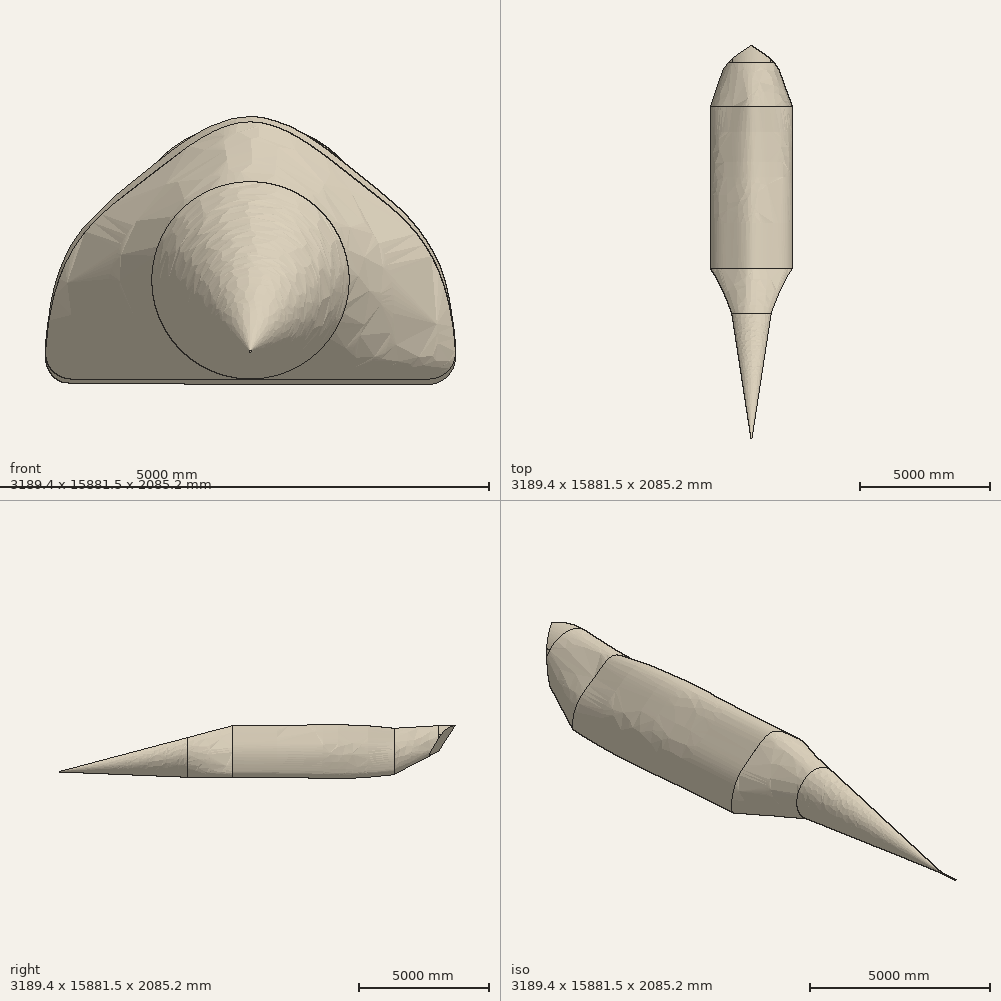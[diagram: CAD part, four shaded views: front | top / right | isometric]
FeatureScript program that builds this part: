
annotation { "Feature Type Name" : "Feature", "Feature Type Description" : "" }
export const myFeature = defineFeature(function(context is Context, id is Id, definition is map)
    precondition{}
    {
        {
            var Q0;
            Q0=qCreatedBy(makeId("Front.planeOp"),FACE);
            cPlane(context, id + "F0", {"entities" : qUnion([Q0]), "cplaneType" : CPlaneType.OFFSET, "offset" : 1750 * mm, "width" : 150 * mm, "height" : 150 * mm});
        }
        {
            var Q0;
            Q0=qCreatedBy(id+"F0.planeOp",FACE);
            var sketch = newSketch(context, id + "F1", { "sketchPlane" : qUnion([Q0])});
            skLineSegment(sketch, "E0.top", {"start": v(-1394.2, -1000) * mm, "end": v(1394.2, -1000) * mm});
            skPoint(sketch, "E0.middle", {"position": v(0, 0) * mm});
            skFitSpline(sketch, "E1", {"points": [v(-1600, -1000) * mm, v(-848, 530) * mm, v(0, 1000) * mm, v(848, 530) * mm, v(1600, -1000) * mm], "startDerivative": vector(0, 10524.75) * mm, "endDerivative": vector(0, -10524.75) * mm});
            skArc(sketch, "E2", {"start": v(-735.27, 618.52) * mm, "mid": v(-1273.27, 435.52) * mm, "end": v(-1440.68, -107.53) * mm});
            skArc(sketch, "E3", {"start": v(1440.68, -107.53) * mm, "mid": v(1273.27, 435.52) * mm, "end": v(735.27, 618.52) * mm});
            skFitSpline(sketch, "E4.trimOffspring", {"points": [v(-1600, -1000) * mm, v(-848, 530) * mm, v(0, 1000) * mm, v(848, 530) * mm, v(1600, -1000) * mm], "startDerivative": vector(0, 10524.75) * mm, "endDerivative": vector(0, -10524.75) * mm});
            skFitSpline(sketch, "E5.trimOffspring", {"points": [v(-1600, -1000) * mm, v(-848, 530) * mm, v(0, 1000) * mm, v(848, 530) * mm, v(1600, -1000) * mm], "startDerivative": vector(0, 10524.75) * mm, "endDerivative": vector(0, -10524.75) * mm});
            skArc(sketch, "E6.filletArc", {"start": v(-1593.82, -787.83) * mm, "mid": v(-1539.85, -937.05) * mm, "end": v(-1394.2, -1000) * mm});
            skArc(sketch, "E7.filletArc", {"start": v(1394.2, -1000) * mm, "mid": v(1539.85, -937.05) * mm, "end": v(1593.82, -787.83) * mm});
            skSolve(sketch);
        }
        {
            var Q0;
            Q0=qCreatedBy(makeId("Front.planeOp"),FACE);
            var sketch = newSketch(context, id + "F2", { "sketchPlane" : qUnion([Q0])});
            skLineSegment(sketch, "E8.top", {"start": v(-1394.2, -1000) * mm, "end": v(1394.2, -1000) * mm});
            skPoint(sketch, "E8.middle", {"position": v(0, 0) * mm});
            skFitSpline(sketch, "E9", {"points": [v(-1600, -1000) * mm, v(-848, 530) * mm, v(0, 1000) * mm, v(848, 530) * mm, v(1600, -1000) * mm], "startDerivative": vector(0, 10524.75) * mm, "endDerivative": vector(0, -10524.75) * mm});
            skArc(sketch, "E10", {"start": v(-735.27, 618.52) * mm, "mid": v(-1273.27, 435.52) * mm, "end": v(-1440.68, -107.53) * mm});
            skArc(sketch, "E11", {"start": v(1440.68, -107.53) * mm, "mid": v(1273.27, 435.52) * mm, "end": v(735.27, 618.52) * mm});
            skFitSpline(sketch, "E12.trimOffspring", {"points": [v(-1600, -1000) * mm, v(-848, 530) * mm, v(0, 1000) * mm, v(848, 530) * mm, v(1600, -1000) * mm], "startDerivative": vector(0, 10524.75) * mm, "endDerivative": vector(0, -10524.75) * mm});
            skFitSpline(sketch, "E13.trimOffspring", {"points": [v(-1600, -1000) * mm, v(-848, 530) * mm, v(0, 1000) * mm, v(848, 530) * mm, v(1600, -1000) * mm], "startDerivative": vector(0, 10524.75) * mm, "endDerivative": vector(0, -10524.75) * mm});
            skArc(sketch, "E14.filletArc", {"start": v(-1593.82, -787.83) * mm, "mid": v(-1539.85, -937.05) * mm, "end": v(-1394.2, -1000) * mm});
            skArc(sketch, "E15.filletArc", {"start": v(1394.2, -1000) * mm, "mid": v(1539.85, -937.05) * mm, "end": v(1593.82, -787.83) * mm});
            skSolve(sketch);
        }
        {
            var Q0;
            Q0=qCreatedBy(makeId("Front.planeOp"),FACE);
            cPlane(context, id + "F3", {"entities" : qUnion([Q0]), "cplaneType" : CPlaneType.OFFSET, "offset" : 3500 * mm, "oppositeDirection" : true, "width" : 150 * mm, "height" : 150 * mm});
        }
        {
            var Q0;
            Q0=qCreatedBy(id+"F3.planeOp",FACE);
            var sketch = newSketch(context, id + "F4", { "sketchPlane" : qUnion([Q0])});
            skLineSegment(sketch, "E16.top", {"start": v(-1394.2, -1000) * mm, "end": v(1394.2, -1000) * mm});
            skPoint(sketch, "E16.middle", {"position": v(0, 0) * mm});
            skFitSpline(sketch, "E17", {"points": [v(-1600, -1000) * mm, v(-848, 530) * mm, v(0, 1000) * mm, v(848, 530) * mm, v(1600, -1000) * mm], "startDerivative": vector(0, 10524.75) * mm, "endDerivative": vector(0, -10524.75) * mm});
            skArc(sketch, "E18", {"start": v(-735.27, 618.52) * mm, "mid": v(-1273.27, 435.52) * mm, "end": v(-1440.68, -107.53) * mm});
            skArc(sketch, "E19", {"start": v(1440.68, -107.53) * mm, "mid": v(1273.27, 435.52) * mm, "end": v(735.27, 618.52) * mm});
            skFitSpline(sketch, "E20.trimOffspring", {"points": [v(-1600, -1000) * mm, v(-848, 530) * mm, v(0, 1000) * mm, v(848, 530) * mm, v(1600, -1000) * mm], "startDerivative": vector(0, 10524.75) * mm, "endDerivative": vector(0, -10524.75) * mm});
            skFitSpline(sketch, "E21.trimOffspring", {"points": [v(-1600, -1000) * mm, v(-848, 530) * mm, v(0, 1000) * mm, v(848, 530) * mm, v(1600, -1000) * mm], "startDerivative": vector(0, 10524.75) * mm, "endDerivative": vector(0, -10524.75) * mm});
            skArc(sketch, "E22.filletArc", {"start": v(-1593.82, -787.83) * mm, "mid": v(-1539.85, -937.05) * mm, "end": v(-1394.2, -1000) * mm});
            skArc(sketch, "E23.filletArc", {"start": v(1394.2, -1000) * mm, "mid": v(1539.85, -937.05) * mm, "end": v(1593.82, -787.83) * mm});
            skSolve(sketch);
        }
        {
            var Q0;
            Q0=qCreatedBy(makeId("Front.planeOp"),FACE);
            cPlane(context, id + "F5", {"entities" : qUnion([Q0]), "cplaneType" : CPlaneType.OFFSET, "offset" : 4500 * mm, "oppositeDirection" : true, "width" : 150 * mm, "height" : 150 * mm});
        }
        {
            var Q0;
            Q0=qCreatedBy(id+"F5.planeOp",FACE);
            var sketch = newSketch(context, id + "F6", { "sketchPlane" : qUnion([Q0])});
            skLineSegment(sketch, "E24.top", {"start": v(-1413.07, -900) * mm, "end": v(1413.07, -900) * mm});
            skPoint(sketch, "E24.middle", {"position": v(0, 0) * mm});
            skFitSpline(sketch, "E25", {"points": [v(-1600, -900) * mm, v(-784.42, 441.24) * mm, v(0, 900) * mm, v(784.42, 441.24) * mm, v(1600, -900) * mm], "startDerivative": vector(0, 9508.62) * mm, "endDerivative": vector(0, -9508.62) * mm});
            skArc(sketch, "E26", {"start": v(-719.25, 488.69) * mm, "mid": v(-1131.76, 394.84) * mm, "end": v(-1324.66, 18.33) * mm});
            skArc(sketch, "E27", {"start": v(1324.66, 18.33) * mm, "mid": v(1131.76, 394.84) * mm, "end": v(719.25, 488.69) * mm});
            skFitSpline(sketch, "E28.trimOffspring", {"points": [v(-1600, -900) * mm, v(-784.42, 441.24) * mm, v(0, 900) * mm, v(784.42, 441.24) * mm, v(1600, -900) * mm], "startDerivative": vector(0, 9508.62) * mm, "endDerivative": vector(0, -9508.62) * mm});
            skFitSpline(sketch, "E29.trimOffspring", {"points": [v(-1600, -900) * mm, v(-784.42, 441.24) * mm, v(0, 900) * mm, v(784.42, 441.24) * mm, v(1600, -900) * mm], "startDerivative": vector(0, 9508.62) * mm, "endDerivative": vector(0, -9508.62) * mm});
            skArc(sketch, "E30.filletArc", {"start": v(-1592.48, -705.43) * mm, "mid": v(-1545.4, -842.02) * mm, "end": v(-1413.07, -900) * mm});
            skArc(sketch, "E31.filletArc", {"start": v(1413.07, -900) * mm, "mid": v(1545.4, -842.02) * mm, "end": v(1592.48, -705.43) * mm});
            skLineSegment(sketch, "E32", {"start": v(-1324.66, 18.33) * mm, "end": v(-719.25, 488.69) * mm, "construction": true});
            skLineSegment(sketch, "E33", {"start": v(1324.66, 18.33) * mm, "end": v(719.25, 488.69) * mm, "construction": true});
            skSolve(sketch);
        }
        {
            var Q0;
            Q0=qCreatedBy(makeId("Front.planeOp"),FACE);
            cPlane(context, id + "F7", {"entities" : qUnion([Q0]), "cplaneType" : CPlaneType.OFFSET, "offset" : 6232.05 * mm, "oppositeDirection" : true, "width" : 150 * mm, "height" : 150 * mm});
        }
        {
            var Q0;
            Q0=qCreatedBy(id+"F7.planeOp",FACE);
            var sketch = newSketch(context, id + "F8", { "sketchPlane" : qUnion([Q0])});
            skArc(sketch, "E34", {"start": v(998.61, 52.63) * mm, "mid": v(0, 1000) * mm, "end": v(-998.61, 52.63) * mm});
            skLineSegment(sketch, "E35", {"start": v(0, 0) * mm, "end": v(-948.68, 0) * mm});
            skLineSegment(sketch, "E36", {"start": v(0, 0) * mm, "end": v(948.68, 0) * mm});
            skLineSegment(sketch, "E37", {"start": v(0, 1000) * mm, "end": v(0, 675) * mm, "construction": true});
            skLineSegment(sketch, "E38", {"start": v(0, 675) * mm, "end": v(-737.82, 675) * mm, "construction": true});
            skLineSegment(sketch, "E39", {"start": v(0, 675) * mm, "end": v(737.82, 675) * mm, "construction": true});
            skPoint(sketch, "E40.visualSharp", {"position": v(-1000, 0) * mm});
            skArc(sketch, "E40.filletArc", {"start": v(-998.61, 52.63) * mm, "mid": v(-984.96, 15.59) * mm, "end": v(-948.68, 0) * mm});
            skPoint(sketch, "E41.visualSharp", {"position": v(1000, 0) * mm});
            skArc(sketch, "E41.filletArc", {"start": v(948.68, 0) * mm, "mid": v(984.96, 15.59) * mm, "end": v(998.61, 52.63) * mm});
            skSolve(sketch);
        }
        {
            var Q0;
            Q0=makeQuery(id+"F1.imprint","IMPRINT",FACE,{"disambiguationData":[TD([[makeQuery(id+"F1.imprint","IMPRINT",EDGE,{"derivedFrom":sQuery(id+"F1.wireOp",EDGE,"E0.top")}),1.0]])]});
            var Q1;
            Q1=makeQuery(id+"F2.imprint","IMPRINT",FACE,{"disambiguationData":[TD([[makeQuery(id+"F2.imprint","IMPRINT",EDGE,{"derivedFrom":sQuery(id+"F2.wireOp",EDGE,"E8.top")}),1.0]])]});
            var Q2;
            Q2=makeQuery(id+"F4.imprint","IMPRINT",FACE,{"disambiguationData":[TD([[makeQuery(id+"F4.imprint","IMPRINT",EDGE,{"derivedFrom":sQuery(id+"F4.wireOp",EDGE,"E16.top")}),1.0]])]});
            var Q3;
            Q3=makeQuery(id+"F6.imprint","IMPRINT",FACE,{"disambiguationData":[TD([[makeQuery(id+"F6.imprint","IMPRINT",EDGE,{"derivedFrom":sQuery(id+"F6.wireOp",EDGE,"E24.top")}),1.0]])]});
            loft(context, id + "F9", {"sheetProfilesArray" : [{ "sheetProfileEntities" : qUnion([Q0]) }, { "sheetProfileEntities" : qUnion([Q1]) }, { "sheetProfileEntities" : qUnion([Q2]) }, { "sheetProfileEntities" : qUnion([Q3]) }]});
        }
        {
            var Q0;
            Q0=sQuery(id+"F6.wireOp",EDGE,"E32");
            var Q1;
            Q1=sQuery(id+"F8.wireOp",VERTEX,"E38.end");
            cPlane(context, id + "F10", {"entities" : qUnion([Q0, Q1]), "cplaneType" : CPlaneType.LINE_ANGLE, "offset" : 25 * mm, "angle" : 0 * degree, "width" : 150 * mm, "height" : 150 * mm});
        }
        {
            var Q0;
            Q0=qCreatedBy(id+"F10.planeOp",FACE);
            var sketch = newSketch(context, id + "F11", { "sketchPlane" : qUnion([Q0])});
            skLineSegment(sketch, "E42", {"start": v(-589.34, 4526.34) * mm, "end": v(-612.8, 6268.32) * mm});
            skLineSegment(sketch, "E43", {"start": v(-1354.08, 4472.19) * mm, "end": v(-612.8, 6268.32) * mm});
            skSolve(sketch);
        }
        {
            var Q0;
            Q0=sQuery(id+"F6.wireOp",EDGE,"E33");
            var Q1;
            Q1=sQuery(id+"F8.wireOp",VERTEX,"E39.end");
            cPlane(context, id + "F12", {"entities" : qUnion([Q0, Q1]), "cplaneType" : CPlaneType.LINE_ANGLE, "offset" : 25 * mm, "angle" : 0 * degree, "width" : 150 * mm, "height" : 150 * mm});
        }
        {
            var Q0;
            Q0=qCreatedBy(id+"F12.planeOp",FACE);
            var sketch = newSketch(context, id + "F13", { "sketchPlane" : qUnion([Q0])});
            skLineSegment(sketch, "E44", {"start": v(589.34, -4526.34) * mm, "end": v(612.8, -6268.32) * mm});
            skLineSegment(sketch, "E45", {"start": v(1354.08, -4472.19) * mm, "end": v(612.8, -6268.32) * mm});
            skSolve(sketch);
        }
        {
            var Q1;
            Q1=makeQuery(id+"F9.opLoft","CAP_FACE",FACE,{"disambiguationData":[OSD([makeQuery(id+"F6.imprint","IMPRINT",FACE,{"disambiguationData":[TD([[makeQuery(id+"F6.imprint","IMPRINT",EDGE,{"derivedFrom":sQuery(id+"F6.wireOp",EDGE,"E24.top")}),1.0]])]})])],"isStart":true});
            var Q2;
            Q2=makeQuery(id+"F8.imprint","IMPRINT",FACE,{"disambiguationData":[TD([[makeQuery(id+"F8.imprint","IMPRINT",EDGE,{"derivedFrom":sQuery(id+"F8.wireOp",EDGE,"E34")}),1.0]])]});
            var Q3;
            Q3=sQuery(id+"F11.wireOp",EDGE,"E42");
            var Q4;
            Q4=sQuery(id+"F13.wireOp",EDGE,"E44");
            loft(context, id + "F14", {"operationType" : NewBodyOperationType.ADD, "addGuides" : true, "sheetProfilesArray" : [{ "sheetProfileEntities" : qUnion([Q1]) }, { "sheetProfileEntities" : qUnion([Q2]) }], "guidesArray" : [{ "guideEntities" : qUnion([Q3]), "guideDerivativeType" : LoftGuideDerivativeType.DEFAULT, "guideDerivativeMagnitude" : 1 }, { "guideEntities" : qUnion([Q4]), "guideDerivativeType" : LoftGuideDerivativeType.DEFAULT, "guideDerivativeMagnitude" : 1 }]});
        }
        {
            var Q0;
            Q0=makeQuery(id+"F14.opLoft","CAP_FACE",FACE,{"disambiguationData":[OSD([makeQuery(id+"F8.imprint","IMPRINT",FACE,{"disambiguationData":[TD([[makeQuery(id+"F8.imprint","IMPRINT",EDGE,{"derivedFrom":sQuery(id+"F8.wireOp",EDGE,"E34")}),1.0]])]})])],"isStart":true});
            extrude(context, id + "F15", {"entities" : qUnion([Q0]), "operationType" : NewBodyOperationType.ADD, "depth" : 649.4 * mm, "offsetDistance" : 25 * mm});
        }
        {
            var Q0;
            Q0=qCreatedBy(makeId("Right.planeOp"),FACE);
            var sketch = newSketch(context, id + "F16", { "sketchPlane" : qUnion([Q0])});
            skLineSegment(sketch, "E46", {"start": v(0, 0) * mm, "end": v(4500, 0) * mm});
            skLineSegment(sketch, "E47", {"start": v(4500, 0) * mm, "end": v(6232.05, 0) * mm});
            skLineSegment(sketch, "E48", {"start": v(4500, 0) * mm, "end": v(4500, 1000) * mm});
            skLineSegment(sketch, "E49", {"start": v(4500, 1000) * mm, "end": v(6881.46, 1000) * mm});
            skLineSegment(sketch, "E50", {"start": v(6881.46, 1000) * mm, "end": v(6881.46, -1000) * mm});
            skLineSegment(sketch, "E51", {"start": v(6881.46, 1000) * mm, "end": v(6232.05, 0) * mm});
            skLineSegment(sketch, "E52", {"start": v(6232.05, 0) * mm, "end": v(5582.64, -1000) * mm});
            skLineSegment(sketch, "E53", {"start": v(5582.64, -1000) * mm, "end": v(6881.46, -1000) * mm});
            skSolve(sketch);
        }
        {
            var Q0;
            Q0=makeQuery(id+"F16.imprint","IMPRINT",FACE,{"disambiguationData":[TD([[makeQuery(id+"F16.imprint","IMPRINT",EDGE,{"derivedFrom":sQuery(id+"F16.wireOp",EDGE,"E50")}),-1.0]])]});
            var Q1;
            Q1=sQuery(id+"F16.wireOp",EDGE,"E49");
            revolve(context, id + "F17", {"operationType" : NewBodyOperationType.REMOVE, "entities" : qUnion([Q0]), "axis" : qUnion([Q1]), "revolveType" : RevolveType.SYMMETRIC, "oppositeDirection" : true, "angle" : 182 * degree});
        }
        {
            var Q0;
            Q0=qCreatedBy(id+"F0.planeOp",FACE);
            var sketch = newSketch(context, id + "F18", { "sketchPlane" : qUnion([Q0])});
            skLineSegment(sketch, "E54.top", {"start": v(-1394.2, -1000) * mm, "end": v(1394.2, -1000) * mm});
            skPoint(sketch, "E54.middle", {"position": v(0, 0) * mm});
            skFitSpline(sketch, "E55", {"points": [v(-1600, -1000) * mm, v(-848, 530) * mm, v(0, 1000) * mm, v(848, 530) * mm, v(1600, -1000) * mm], "startDerivative": vector(0, 10524.75) * mm, "endDerivative": vector(0, -10524.75) * mm});
            skArc(sketch, "E56.filletArc", {"start": v(-1593.82, -787.83) * mm, "mid": v(-1539.85, -937.05) * mm, "end": v(-1394.2, -1000) * mm});
            skArc(sketch, "E57.filletArc", {"start": v(1394.2, -1000) * mm, "mid": v(1539.85, -937.05) * mm, "end": v(1593.82, -787.83) * mm});
            skLineSegment(sketch, "E58", {"start": v(-1593.82, -787.83) * mm, "end": v(-1394.2, -1000) * mm, "construction": true});
            skLineSegment(sketch, "E59", {"start": v(1593.82, -787.83) * mm, "end": v(1394.2, -1000) * mm, "construction": true});
            skSolve(sketch);
        }
        {
            var Q0;
            Q0=qCreatedBy(makeId("Right.planeOp"),FACE);
            var sketch = newSketch(context, id + "F19", { "sketchPlane" : qUnion([Q0])});
            skLineSegment(sketch, "E60", {"start": v(0, 0) * mm, "end": v(-1750, 0) * mm});
            skLineSegment(sketch, "E61", {"start": v(-1750, 0) * mm, "end": v(-3500, 0) * mm});
            skLineSegment(sketch, "E62", {"start": v(-3500, 0) * mm, "end": v(-3500, -1000) * mm});
            skLineSegment(sketch, "E63", {"start": v(-3500, -1000) * mm, "end": v(-8500, -1000) * mm});
            skLineSegment(sketch, "E64", {"start": v(-8500, -1000) * mm, "end": v(-8500, -792.04) * mm});
            skLineSegment(sketch, "E65", {"start": v(-1750, 0) * mm, "end": v(-1750, 1000) * mm});
            skLineSegment(sketch, "E66", {"start": v(-1750, 1000) * mm, "end": v(-8500, -792.04) * mm});
            skLineSegment(sketch, "E67", {"start": v(-8500, -792.04) * mm, "end": v(-3500, -1000) * mm});
            skLineSegment(sketch, "E68", {"start": v(-3500, 0) * mm, "end": v(-3500, 535.4) * mm});
            skLineSegment(sketch, "E69", {"start": v(-8500, -792.04) * mm, "end": v(-8450, -792.04) * mm});
            skLineSegment(sketch, "E70", {"start": v(-8450, -792.04) * mm, "end": v(-8450, -778.76) * mm});
            skLineSegment(sketch, "E71", {"start": v(-8450, -792.04) * mm, "end": v(-8450, -794.12) * mm});
            skSolve(sketch);
        }
        {
            var Q0;
            Q0=qCreatedBy(makeId("Front.planeOp"),FACE);
            cPlane(context, id + "F20", {"entities" : qUnion([Q0]), "cplaneType" : CPlaneType.OFFSET, "offset" : 3500 * mm, "width" : 150 * mm, "height" : 150 * mm});
        }
        {
            var Q0;
            Q0=qCreatedBy(id+"F20.planeOp",FACE);
            var sketch = newSketch(context, id + "F21", { "sketchPlane" : qUnion([Q0])});
            skCircle(sketch, "E72", {"center": v(0, -232.3) * mm, "radius": 767.7 * mm});
            skLineSegment(sketch, "E73", {"start": v(0, -1000) * mm, "end": v(0, -800) * mm, "construction": true});
            skLineSegment(sketch, "E74", {"start": v(0, -800) * mm, "end": v(-516.8, -800) * mm, "construction": true});
            skLineSegment(sketch, "E75", {"start": v(0, -800) * mm, "end": v(516.8, -800) * mm, "construction": true});
            skSolve(sketch);
        }
        {
            var Q0;
            Q0=qCreatedBy(makeId("Front.planeOp"),FACE);
            cPlane(context, id + "F22", {"entities" : qUnion([Q0]), "cplaneType" : CPlaneType.OFFSET, "offset" : 8450 * mm, "width" : 150 * mm, "height" : 150 * mm});
        }
        {
            var Q0;
            Q0=qCreatedBy(id+"F22.planeOp",FACE);
            var sketch = newSketch(context, id + "F23", { "sketchPlane" : qUnion([Q0])});
            skCircle(sketch, "E76", {"center": v(0, -786.44) * mm, "radius": 7.68 * mm});
            skSolve(sketch);
        }
        {
            var Q0;
            Q0=sQuery(id+"F18.wireOp",EDGE,"E58");
            var Q1;
            Q1=sQuery(id+"F21.wireOp",VERTEX,"E74.end");
            cPlane(context, id + "F24", {"entities" : qUnion([Q0, Q1]), "cplaneType" : CPlaneType.LINE_ANGLE, "offset" : 25 * mm, "angle" : 0 * degree, "width" : 150 * mm, "height" : 150 * mm});
        }
        {
            var Q0;
            Q0=qCreatedBy(id+"F24.planeOp",FACE);
            var sketch = newSketch(context, id + "F25", { "sketchPlane" : qUnion([Q0])});
            skLineSegment(sketch, "E77", {"start": v(910.33, 518.4) * mm, "end": v(2824.69, -228.5) * mm});
            skLineSegment(sketch, "E78", {"start": v(2824.69, -228.5) * mm, "end": v(910.33, 227.09) * mm});
            skSolve(sketch);
        }
        {
            var Q0;
            Q0=sQuery(id+"F18.wireOp",EDGE,"E59");
            var Q1;
            Q1=sQuery(id+"F21.wireOp",VERTEX,"E75.end");
            cPlane(context, id + "F26", {"entities" : qUnion([Q0, Q1]), "cplaneType" : CPlaneType.LINE_ANGLE, "offset" : 25 * mm, "angle" : 0 * degree, "width" : 150 * mm, "height" : 150 * mm});
        }
        {
            var Q0;
            Q0=qCreatedBy(id+"F26.planeOp",FACE);
            var sketch = newSketch(context, id + "F27", { "sketchPlane" : qUnion([Q0])});
            skLineSegment(sketch, "E79", {"start": v(2824.69, -228.5) * mm, "end": v(910.33, 518.4) * mm});
            skLineSegment(sketch, "E80", {"start": v(2824.69, -228.5) * mm, "end": v(910.33, 227.09) * mm});
            skSolve(sketch);
        }
        {
            var Q1;
            Q1=makeQuery(id+"F18.imprint","IMPRINT",FACE,{"disambiguationData":[TD([[makeQuery(id+"F18.imprint","IMPRINT",EDGE,{"derivedFrom":sQuery(id+"F18.wireOp",EDGE,"E54.top")}),1.0]])]});
            var Q2;
            Q2=makeQuery(id+"F21.imprint","IMPRINT",FACE,{"disambiguationData":[TD([[makeQuery(id+"F21.imprint","IMPRINT",EDGE,{"derivedFrom":sQuery(id+"F21.wireOp",EDGE,"E72")}),1.0]])]});
            var Q3;
            Q3=sQuery(id+"F25.wireOp",EDGE,"E77");
            var Q4;
            Q4=sQuery(id+"F27.wireOp",EDGE,"E79");
            loft(context, id + "F28", {"addGuides" : true, "sheetProfilesArray" : [{ "sheetProfileEntities" : qUnion([Q1]) }, { "sheetProfileEntities" : qUnion([Q2]) }], "guidesArray" : [{ "guideEntities" : qUnion([Q3]), "guideDerivativeType" : LoftGuideDerivativeType.DEFAULT, "guideDerivativeMagnitude" : 1 }, { "guideEntities" : qUnion([Q4]), "guideDerivativeType" : LoftGuideDerivativeType.DEFAULT, "guideDerivativeMagnitude" : 1 }]});
        }
        {
            var Q1;
            Q1=makeQuery(id+"F28.opLoft","CAP_FACE",FACE,{"disambiguationData":[OSD([makeQuery(id+"F21.imprint","IMPRINT",FACE,{"disambiguationData":[TD([[makeQuery(id+"F21.imprint","IMPRINT",EDGE,{"derivedFrom":sQuery(id+"F21.wireOp",EDGE,"E72")}),1.0]])]})])],"isStart":true});
            var Q2;
            Q2=makeQuery(id+"F23.imprint","IMPRINT",FACE,{"disambiguationData":[TD([[makeQuery(id+"F23.imprint","IMPRINT",EDGE,{"derivedFrom":sQuery(id+"F23.wireOp",EDGE,"E76")}),1.0]])]});
            loft(context, id + "F29", {"operationType" : NewBodyOperationType.ADD, "sheetProfilesArray" : [{ "sheetProfileEntities" : qUnion([Q1]) }, { "sheetProfileEntities" : qUnion([Q2]) }]});
        }
        {
            var Q0;
            Q0=makeQuery(id+"F29.opLoft","CAP_FACE",FACE,{"disambiguationData":[OSD([makeQuery(id+"F23.imprint","IMPRINT",FACE,{"disambiguationData":[TD([[makeQuery(id+"F23.imprint","IMPRINT",EDGE,{"derivedFrom":sQuery(id+"F23.wireOp",EDGE,"E76")}),1.0]])]})])],"isStart":true});
            extrude(context, id + "F30", {"entities" : qUnion([Q0]), "operationType" : NewBodyOperationType.ADD, "depth" : 550 * mm, "offsetDistance" : 25 * mm});
        }
    });
